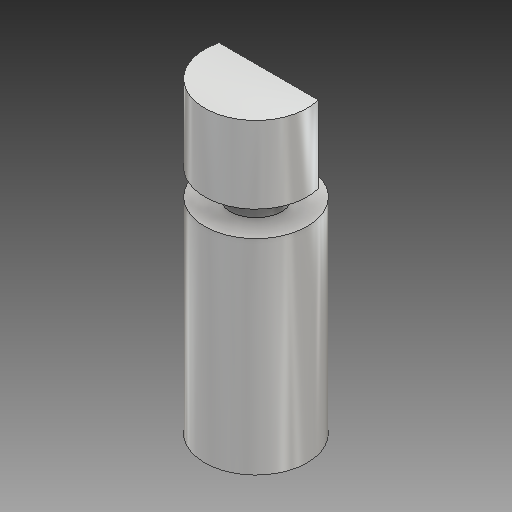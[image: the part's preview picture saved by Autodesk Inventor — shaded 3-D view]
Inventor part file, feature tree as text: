
AUTODESK INVENTOR PART (.ipt)
format: ipt  version: 2019 (Build 230136000, 136)  size: 119,296 bytes
history: native  units: mm
features: extrude x3, sketch x3, plane x1, projected_geometry x1
ambient origin geometry x8: Origin, YZ Plane, XZ Plane, XY Plane, X Axis, Y Axis, Z Axis, Center Point
bodies: Volumenkörper1 (feature_tree)
feature tree (8):
  extrude  "Extrusion1"  Depth=12.0mm TaperAngle=0.0deg
  extrude  "Extrusion2"  [1 undecoded]
  plane  "Arbeitsebene1"
  extrude  "Extrusion3"  Depth=1.0mm TaperAngle=0.0deg
  sketch  "Skizze1"  dims[d0=4.0mm d1=12.0mm d2=0.0mm]
  sketch  "Skizze2"  dims[d3=3.0mm d4=0.0mm d5=-3.0mm]
  projected_geometry  "Projizierte Kontur1"
  sketch  "Skizze3"  dims[d6=2.0mm d7=1.0mm d8=0.0mm]
note: 1 required parameter value undecoded (feature->parameter linkage not recoverable at this tier; creation-order binding heuristic only, values carry confidence <= 0.55)
